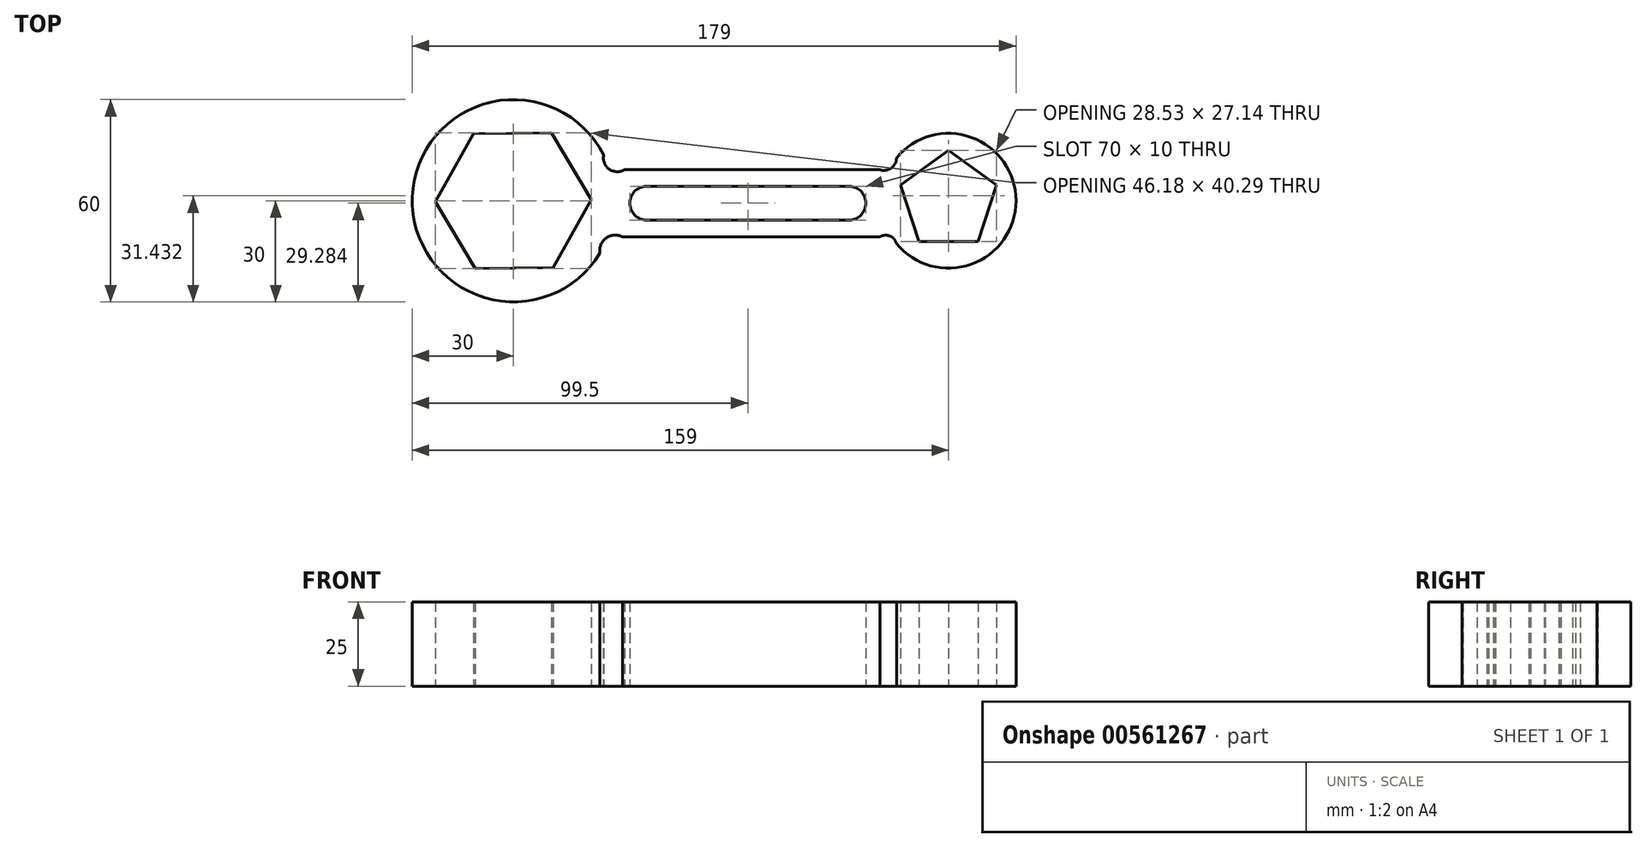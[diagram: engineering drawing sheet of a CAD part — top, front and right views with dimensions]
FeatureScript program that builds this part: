
annotation { "Feature Type Name" : "Feature", "Feature Type Description" : "" }
export const myFeature = defineFeature(function(context is Context, id is Id, definition is map)
    precondition{}
    {
        {
            var Q0;
            Q0=qCreatedBy(makeId("Top.planeOp"),FACE);
            var sketch = newSketch(context, id + "F0", { "sketchPlane" : qUnion([Q0])});
            skCircle(sketch, "E0.cCircle", {"center": v(0, 0) * mm, "radius": 12.14 * mm, "construction": true});
            skLineSegment(sketch, "E0.0", {"start": v(0, 15) * mm, "end": v(14.27, 4.64) * mm});
            skLineSegment(sketch, "E0.1", {"start": v(14.27, 4.64) * mm, "end": v(8.82, -12.14) * mm});
            skLineSegment(sketch, "E0.2", {"start": v(8.82, -12.14) * mm, "end": v(-8.82, -12.14) * mm});
            skLineSegment(sketch, "E0.3", {"start": v(-8.82, -12.14) * mm, "end": v(-14.27, 4.64) * mm});
            skLineSegment(sketch, "E0.4", {"start": v(-14.27, 4.64) * mm, "end": v(0, 15) * mm});
            skPoint(sketch, "E0.0.midPoint", {"position": v(7.13, 9.82) * mm});
            skCircle(sketch, "E1.cCircle", {"center": v(-129, 0) * mm, "radius": 20 * mm, "construction": true});
            skLineSegment(sketch, "E1.0", {"start": v(-117.71, 20.15) * mm, "end": v(-105.9, 0.3) * mm});
            skLineSegment(sketch, "E1.1", {"start": v(-105.9, 0.3) * mm, "end": v(-117.2, -19.85) * mm});
            skLineSegment(sketch, "E1.2", {"start": v(-117.2, -19.85) * mm, "end": v(-140.29, -20.15) * mm});
            skLineSegment(sketch, "E1.3", {"start": v(-140.29, -20.15) * mm, "end": v(-152.1, -0.3) * mm});
            skLineSegment(sketch, "E1.4", {"start": v(-152.1, -0.3) * mm, "end": v(-140.8, 19.85) * mm});
            skLineSegment(sketch, "E1.5", {"start": v(-140.8, 19.85) * mm, "end": v(-117.71, 20.15) * mm});
            skPoint(sketch, "E1.0.midPoint", {"position": v(-111.8, 10.22) * mm});
            skArc(sketch, "E2", {"start": v(-102.25, 13.57) * mm, "mid": v(-158.98, 1.13) * mm, "end": v(-103.34, -15.54) * mm});
            skArc(sketch, "E3", {"start": v(-15.43, -12.73) * mm, "mid": v(20, 0) * mm, "end": v(-15.43, 12.73) * mm});
            skLineSegment(sketch, "E4", {"start": v(-109, 0) * mm, "end": v(-106.07, 0) * mm});
            skLineSegment(sketch, "E5", {"start": v(-96.02, 9.28) * mm, "end": v(-20.55, 9.28) * mm});
            skLineSegment(sketch, "E6", {"start": v(-96.7, -10.72) * mm, "end": v(-20.31, -10.72) * mm});
            skLineSegment(sketch, "E7", {"start": v(-89.5, 4.28) * mm, "end": v(-29.5, 4.28) * mm});
            skLineSegment(sketch, "E8", {"start": v(-24.5, -0.72) * mm, "end": v(-24.5, -0.72) * mm});
            skLineSegment(sketch, "E9", {"start": v(-29.5, -5.72) * mm, "end": v(-89.5, -5.72) * mm});
            skLineSegment(sketch, "E10", {"start": v(-94.5, -0.72) * mm, "end": v(-94.5, -0.72) * mm});
            skPoint(sketch, "E11.visualSharp", {"position": v(-24.5, 4.28) * mm});
            skArc(sketch, "E11.filletArc", {"start": v(-24.5, -0.72) * mm, "mid": v(-25.96, 2.82) * mm, "end": v(-29.5, 4.28) * mm});
            skPoint(sketch, "E12.visualSharp", {"position": v(-24.5, -5.72) * mm});
            skArc(sketch, "E12.filletArc", {"start": v(-29.5, -5.72) * mm, "mid": v(-25.96, -4.25) * mm, "end": v(-24.5, -0.72) * mm});
            skPoint(sketch, "E13.visualSharp", {"position": v(-94.5, 4.28) * mm});
            skArc(sketch, "E13.filletArc", {"start": v(-89.5, 4.28) * mm, "mid": v(-93.04, 2.82) * mm, "end": v(-94.5, -0.72) * mm});
            skPoint(sketch, "E14.visualSharp", {"position": v(-94.5, -5.72) * mm});
            skArc(sketch, "E14.filletArc", {"start": v(-94.5, -0.72) * mm, "mid": v(-93.04, -4.25) * mm, "end": v(-89.5, -5.72) * mm});
            skLineSegment(sketch, "E15.trimOffspring", {"start": v(-12.76, 0) * mm, "end": v(-12.14, 0) * mm});
            skArc(sketch, "E16", {"start": v(-102.25, 13.57) * mm, "mid": v(-100.57, 9.35) * mm, "end": v(-96.02, 9.28) * mm});
            skArc(sketch, "E17", {"start": v(-96.7, -10.72) * mm, "mid": v(-101.52, -11.05) * mm, "end": v(-103.34, -15.54) * mm});
            skArc(sketch, "E18.trimOffspring", {"start": v(-100.98, -10.72) * mm, "mid": v(-99, -0.76) * mm, "end": v(-100.47, 9.28) * mm});
            skArc(sketch, "E19", {"start": v(-20.55, 9.28) * mm, "mid": v(-17.07, 9.63) * mm, "end": v(-15.43, 12.73) * mm});
            skArc(sketch, "E20", {"start": v(-15.43, -12.73) * mm, "mid": v(-17.36, -10.48) * mm, "end": v(-20.31, -10.72) * mm});
            skArc(sketch, "E21.trimOffspring", {"start": v(-17.71, 9.28) * mm, "mid": v(-19.98, -0.83) * mm, "end": v(-16.89, -10.72) * mm});
            skSolve(sketch);
        }
        {
            var Q0;
            Q0=makeQuery(id+"F0.imprint","IMPRINT",FACE,{"disambiguationData":[TD([[makeQuery(id+"F0.imprint","IMPRINT",EDGE,{"derivedFrom":sQuery(id+"F0.wireOp",EDGE,"E0.0")}),1.0]])]});
            var Q1;
            {var subQ4=sQuery(id+"F0.wireOp",EDGE,"E5");Q1=makeQuery(id+"F0.imprint","IMPRINT",FACE,{"disambiguationData":[TD([[makeQuery(id+"F0.imprint","IMPRINT",EDGE,{"derivedFrom":subQ4}),-1.0]])]});}
            var Q2;
            {var subQ4=sQuery(id+"F0.wireOp",EDGE,"E1.0");Q2=makeQuery(id+"F0.imprint","IMPRINT",FACE,{"disambiguationData":[TD([[makeQuery(id+"F0.imprint","IMPRINT",EDGE,{"derivedFrom":subQ4}),1.0]])]});}
            extrude(context, id + "F1", {"entities" : qUnion([Q0, Q1, Q2]), "depth" : 25 * mm, "offsetDistance" : 25 * mm});
        }
    });
